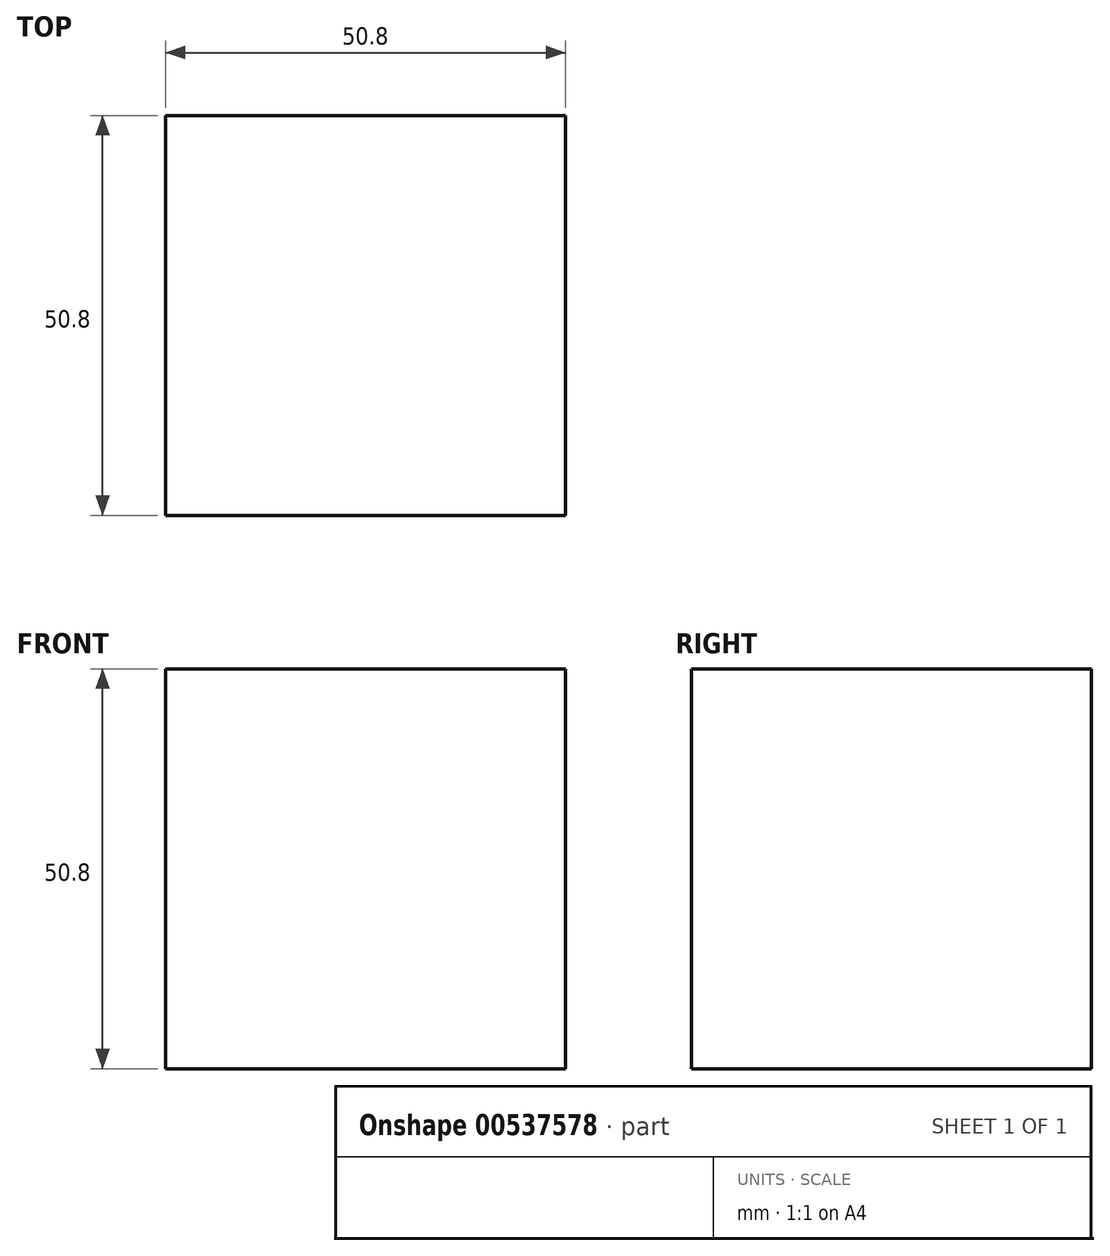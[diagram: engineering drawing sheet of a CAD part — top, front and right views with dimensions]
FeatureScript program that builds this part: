
annotation { "Feature Type Name" : "Feature", "Feature Type Description" : "" }
export const myFeature = defineFeature(function(context is Context, id is Id, definition is map)
    precondition{}
    {
        {
            var Q0;
            Q0=qCreatedBy(makeId("Top.planeOp"),FACE);
            var sketch = newSketch(context, id + "F0", { "sketchPlane" : qUnion([Q0])});
            skLineSegment(sketch, "E0.bottom", {"start": v(25.4, -25.4) * mm, "end": v(-25.4, -25.4) * mm});
            skLineSegment(sketch, "E0.top", {"start": v(25.4, 25.4) * mm, "end": v(-25.4, 25.4) * mm});
            skLineSegment(sketch, "E0.left", {"start": v(25.4, -25.4) * mm, "end": v(25.4, 25.4) * mm});
            skLineSegment(sketch, "E0.right", {"start": v(-25.4, -25.4) * mm, "end": v(-25.4, 25.4) * mm});
            skPoint(sketch, "E0.middle", {"position": v(0, 0) * mm});
            skSolve(sketch);
        }
        {
            var Q0;
            Q0=makeQuery(id+"F0.imprint","IMPRINT",FACE,{"disambiguationData":[TD([[makeQuery(id+"F0.imprint","IMPRINT",EDGE,{"derivedFrom":sQuery(id+"F0.wireOp",EDGE,"E0.bottom")}),-1.0]])]});
            extrude(context, id + "F1", {"entities" : qUnion([Q0]), "depth" : 50.8 * mm, "offsetDistance" : 25.4 * mm});
        }
    });
